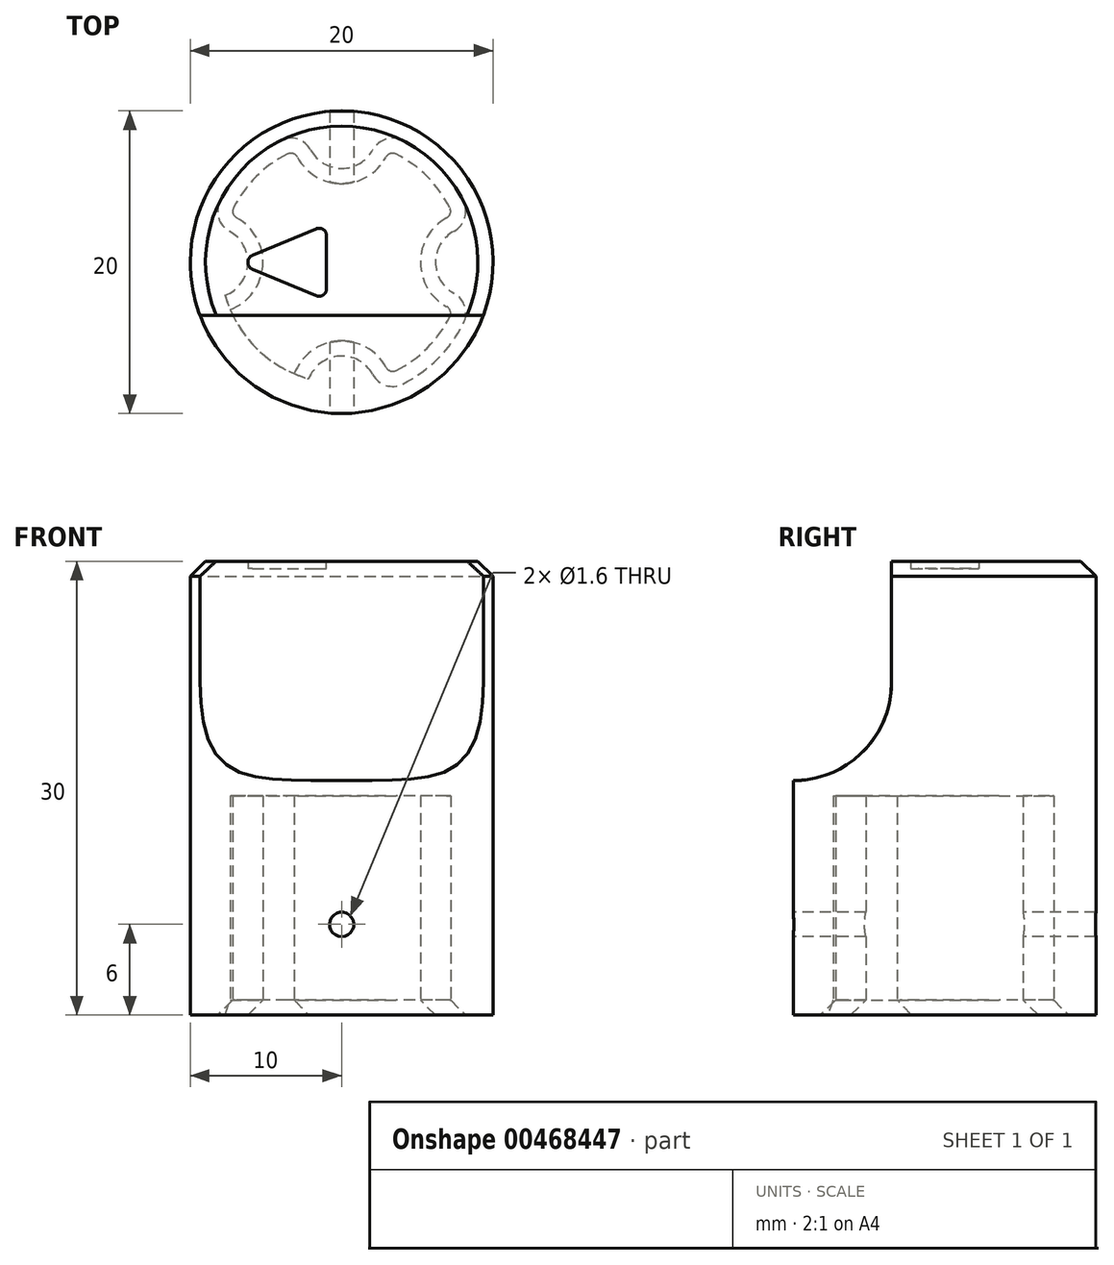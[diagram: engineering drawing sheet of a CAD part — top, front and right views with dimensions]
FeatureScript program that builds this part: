
annotation { "Feature Type Name" : "Feature", "Feature Type Description" : "" }
export const myFeature = defineFeature(function(context is Context, id is Id, definition is map)
    precondition{}
    {
        {
            var Q0;
            Q0=qCreatedBy(makeId("Right.planeOp"),FACE);
            var sketch = newSketch(context, id + "F0", { "sketchPlane" : qUnion([Q0])});
            skLineSegment(sketch, "E0", {"start": v(-8, 0) * mm, "end": v(-8, 14.5) * mm});
            skLineSegment(sketch, "E1", {"start": v(-8, 14.5) * mm, "end": v(0, 14.5) * mm});
            skLineSegment(sketch, "E2", {"start": v(0, 14.5) * mm, "end": v(0, 30) * mm});
            skLineSegment(sketch, "E3", {"start": v(0, 30) * mm, "end": v(-10, 30) * mm});
            skLineSegment(sketch, "E4", {"start": v(-10, 30) * mm, "end": v(-10, 0) * mm});
            skLineSegment(sketch, "E5", {"start": v(-10, 0) * mm, "end": v(-8, 0) * mm});
            skSolve(sketch);
        }
        {
            var Q0;
            Q0=qSketchRegion(id+"F0",true);
            var Q1;
            Q1=sQuery(id+"F0.wireOp",EDGE,"E2");
            revolve(context, id + "F1", {"surfaceOperationType" : NewSurfaceOperationType.NEW, "entities" : qUnion([Q0]), "axis" : qUnion([Q1]), "revolveType" : RevolveType.FULL});
        }
        {
            var Q0;
            Q0=qCreatedBy(makeId("Right.planeOp"),FACE);
            var sketch = newSketch(context, id + "F2", { "sketchPlane" : qUnion([Q0])});
            skLineSegment(sketch, "E6", {"start": v(-3.5, 30) * mm, "end": v(-3.5, 22) * mm});
            skArc(sketch, "E7", {"start": v(-10, 15.5) * mm, "mid": v(-5.4, 17.4) * mm, "end": v(-3.5, 22) * mm});
            skLineSegment(sketch, "E8", {"start": v(-10, 15.5) * mm, "end": v(-10, 30) * mm});
            skLineSegment(sketch, "E9", {"start": v(-10, 30) * mm, "end": v(-3.5, 30) * mm});
            skSolve(sketch);
        }
        {
            var Q0;
            Q0=qSketchRegion(id+"F2",true);
            extrude(context, id + "F3", {"entities" : qUnion([Q0]), "operationType" : NewBodyOperationType.REMOVE, "endBound" : BoundingType.SYMMETRIC, "oppositeDirection" : true, "offsetDistance" : 25 * mm, "depth" : 25 * mm});
        }
        {
            var Q0;
            Q0=makeQuery(id+"FGqc0gzjsB6oOKz_1.1.F3.boolean.opBoolean","SPLIT",EDGE,{"disambiguationData":[OD(1.0)],"derivedFrom":makeQuery(id+"F1.opRevolve","SWEPT_EDGE",EDGE,{"disambiguationData":[OSD([sQuery(id+"F0.wireOp",EDGE,"E3"),sQuery(id+"F0.wireOp",EDGE,"E4")])]})});
            var Q1;
            Q1=makeQuery(id+"FGqc0gzjsB6oOKz_1.1.F3.boolean.opBoolean","SPLIT",EDGE,{"disambiguationData":[OD(0.0)],"derivedFrom":makeQuery(id+"F1.opRevolve","SWEPT_EDGE",EDGE,{"disambiguationData":[OSD([sQuery(id+"F0.wireOp",EDGE,"E3"),sQuery(id+"F0.wireOp",EDGE,"E4")])]})});
            chamfer(context, id + "F4", {"entities" : qUnion([Q0, Q1]), "width" : 1 * mm, "tangentPropagation" : true});
        }
        {
            var Q0;
            Q0=makeQuery(id+"F1.opRevolve","SWEPT_FACE",FACE,{"disambiguationData":[OSD([sQuery(id+"F0.wireOp",EDGE,"E5")])]});
            var sketch = newSketch(context, id + "F5", { "sketchPlane" : qUnion([Q0])});
            skArc(sketch, "E10", {"start": v(-7.37, -3.12) * mm, "mid": v(-5.2, 0) * mm, "end": v(-7.37, 3.12) * mm});
            skArc(sketch, "E11", {"start": v(-3.12, 7.37) * mm, "mid": v(0, 5.2) * mm, "end": v(3.12, 7.37) * mm});
            skArc(sketch, "E12", {"start": v(7.37, 3.12) * mm, "mid": v(5.2, 0) * mm, "end": v(7.37, -3.12) * mm});
            skArc(sketch, "E13", {"start": v(3.12, -7.37) * mm, "mid": v(0, -5.2) * mm, "end": v(-3.12, -7.37) * mm});
            skArc(sketch, "E14.0", {"start": v(-7.37, 3.12) * mm, "mid": v(-8, 0) * mm, "end": v(-7.37, -3.12) * mm});
            skArc(sketch, "E15.trimOffspring", {"start": v(3.12, 7.37) * mm, "mid": v(0, 8) * mm, "end": v(-3.12, 7.37) * mm});
            skArc(sketch, "E16.trimOffspring", {"start": v(7.37, -3.12) * mm, "mid": v(8, 0) * mm, "end": v(7.37, 3.12) * mm});
            skArc(sketch, "E17.trimOffspring", {"start": v(-3.12, -7.37) * mm, "mid": v(0, -8) * mm, "end": v(3.12, -7.37) * mm});
            skSolve(sketch);
        }
        {
            var Q0;
            Q0 = qSketchRegion(id + "F5", true);
            extrude(context, id + "F6", {"entities" : qUnion([Q0]), "operationType" : NewBodyOperationType.ADD, "endBound" : BoundingType.UP_TO_NEXT, "oppositeDirection" : true, "depth" : 25 * mm, "offsetDistance" : 25 * mm});
        }
        {
            var Q0;
            {var subQ0=sQuery(id+"F5.wireOp",EDGE,"E15.trimOffspring");var subQ1=sQuery(id+"F5.wireOp",EDGE,"E11");var subQ2=sQuery(id+"F0.wireOp",EDGE,"E5");var subQ3=sQuery(id+"F0.wireOp",EDGE,"E0");Q0=makeQuery(id+"F6.opExtrude","SWEPT_EDGE",EDGE,{"disambiguationData":[OSD([subQ3,subQ2,subQ1,subQ0]),TDD([makeQuery(id+"F5.imprint","INTERSECT",VERTEX,{"disambiguationData":[OD(0.0)],"derivedFrom":[makeQuery(id+"F1.opRevolve","SWEPT_EDGE",EDGE,{"disambiguationData":[OSD([subQ3,subQ2])]}),subQ1,subQ0]})])]});}
            var Q1;
            {var subQ0=sQuery(id+"F5.wireOp",EDGE,"E14.0");var subQ1=sQuery(id+"F5.wireOp",EDGE,"E10");var subQ2=sQuery(id+"F0.wireOp",EDGE,"E5");var subQ3=sQuery(id+"F0.wireOp",EDGE,"E0");Q1=makeQuery(id+"F6.opExtrude","SWEPT_EDGE",EDGE,{"disambiguationData":[OSD([subQ3,subQ2,subQ1,subQ0]),TDD([makeQuery(id+"F5.imprint","INTERSECT",VERTEX,{"disambiguationData":[OD(1.0)],"derivedFrom":[makeQuery(id+"F1.opRevolve","SWEPT_EDGE",EDGE,{"disambiguationData":[OSD([subQ3,subQ2])]}),subQ1,subQ0]})])]});}
            var Q2;
            {var subQ0=sQuery(id+"F5.wireOp",EDGE,"E14.0");var subQ1=sQuery(id+"F5.wireOp",EDGE,"E10");var subQ2=sQuery(id+"F0.wireOp",EDGE,"E5");var subQ3=sQuery(id+"F0.wireOp",EDGE,"E0");Q2=makeQuery(id+"F6.opExtrude","SWEPT_EDGE",EDGE,{"disambiguationData":[OSD([subQ3,subQ2,subQ1,subQ0]),TDD([makeQuery(id+"F5.imprint","INTERSECT",VERTEX,{"disambiguationData":[OD(0.0)],"derivedFrom":[makeQuery(id+"F1.opRevolve","SWEPT_EDGE",EDGE,{"disambiguationData":[OSD([subQ3,subQ2])]}),subQ1,subQ0]})])]});}
            var Q3;
            {var subQ0=sQuery(id+"F5.wireOp",EDGE,"E17.trimOffspring");var subQ1=sQuery(id+"F5.wireOp",EDGE,"E13");var subQ2=sQuery(id+"F0.wireOp",EDGE,"E5");var subQ3=sQuery(id+"F0.wireOp",EDGE,"E0");Q3=makeQuery(id+"F6.opExtrude","SWEPT_EDGE",EDGE,{"disambiguationData":[OSD([subQ3,subQ2,subQ1,subQ0]),TDD([makeQuery(id+"F5.imprint","INTERSECT",VERTEX,{"disambiguationData":[OD(1.0)],"derivedFrom":[makeQuery(id+"F1.opRevolve","SWEPT_EDGE",EDGE,{"disambiguationData":[OSD([subQ3,subQ2])]}),subQ1,subQ0]})])]});}
            var Q4;
            {var subQ0=sQuery(id+"F5.wireOp",EDGE,"E17.trimOffspring");var subQ1=sQuery(id+"F5.wireOp",EDGE,"E13");var subQ2=sQuery(id+"F0.wireOp",EDGE,"E5");var subQ3=sQuery(id+"F0.wireOp",EDGE,"E0");Q4=makeQuery(id+"F6.opExtrude","SWEPT_EDGE",EDGE,{"disambiguationData":[OSD([subQ3,subQ2,subQ1,subQ0]),TDD([makeQuery(id+"F5.imprint","INTERSECT",VERTEX,{"disambiguationData":[OD(0.0)],"derivedFrom":[makeQuery(id+"F1.opRevolve","SWEPT_EDGE",EDGE,{"disambiguationData":[OSD([subQ3,subQ2])]}),subQ1,subQ0]})])]});}
            var Q5;
            {var subQ0=sQuery(id+"F5.wireOp",EDGE,"E16.trimOffspring");var subQ1=sQuery(id+"F5.wireOp",EDGE,"E12");var subQ2=sQuery(id+"F0.wireOp",EDGE,"E5");var subQ3=sQuery(id+"F0.wireOp",EDGE,"E0");Q5=makeQuery(id+"F6.opExtrude","SWEPT_EDGE",EDGE,{"disambiguationData":[OSD([subQ3,subQ2,subQ1,subQ0]),TDD([makeQuery(id+"F5.imprint","INTERSECT",VERTEX,{"disambiguationData":[OD(1.0)],"derivedFrom":[makeQuery(id+"F1.opRevolve","SWEPT_EDGE",EDGE,{"disambiguationData":[OSD([subQ3,subQ2])]}),subQ1,subQ0]})])]});}
            var Q6;
            {var subQ0=sQuery(id+"F5.wireOp",EDGE,"E16.trimOffspring");var subQ1=sQuery(id+"F5.wireOp",EDGE,"E12");var subQ2=sQuery(id+"F0.wireOp",EDGE,"E5");var subQ3=sQuery(id+"F0.wireOp",EDGE,"E0");Q6=makeQuery(id+"F6.opExtrude","SWEPT_EDGE",EDGE,{"disambiguationData":[OSD([subQ3,subQ2,subQ1,subQ0]),TDD([makeQuery(id+"F5.imprint","INTERSECT",VERTEX,{"disambiguationData":[OD(0.0)],"derivedFrom":[makeQuery(id+"F1.opRevolve","SWEPT_EDGE",EDGE,{"disambiguationData":[OSD([subQ3,subQ2])]}),subQ1,subQ0]})])]});}
            var Q7;
            {var subQ0=sQuery(id+"F5.wireOp",EDGE,"E15.trimOffspring");var subQ1=sQuery(id+"F5.wireOp",EDGE,"E11");var subQ2=sQuery(id+"F0.wireOp",EDGE,"E5");var subQ3=sQuery(id+"F0.wireOp",EDGE,"E0");Q7=makeQuery(id+"F6.opExtrude","SWEPT_EDGE",EDGE,{"disambiguationData":[OSD([subQ3,subQ2,subQ1,subQ0]),TDD([makeQuery(id+"F5.imprint","INTERSECT",VERTEX,{"disambiguationData":[OD(1.0)],"derivedFrom":[makeQuery(id+"F1.opRevolve","SWEPT_EDGE",EDGE,{"disambiguationData":[OSD([subQ3,subQ2])]}),subQ1,subQ0]})])]});}
            fillet(context, id + "F7", {"entities" : qUnion([Q0, Q1, Q2, Q3, Q4, Q5, Q6, Q7]), "tangentPropagation" : true, "radius" : .5 * mm, "defaultsChanged" : true, "vertexSettings" : [], "allowEdgeOverflow" : false});
        }
        {
            var Q0;
            Q0=qCreatedBy(makeId("Front.planeOp"),FACE);
            var sketch = newSketch(context, id + "F8", { "sketchPlane" : qUnion([Q0])});
            skCircle(sketch, "E18", {"center": v(0, 6) * mm, "radius": 0.8 * mm});
            skSolve(sketch);
        }
        {
            var Q0;
            Q0=qSketchRegion(id+"F8",true);
            extrude(context, id + "F9", {"entities" : qUnion([Q0]), "operationType" : NewBodyOperationType.REMOVE, "endBound" : BoundingType.SYMMETRIC, "oppositeDirection" : true, "depth" : 25 * mm, "hasSecondDirection" : true, "secondDirectionBound" : SecondDirectionBoundingType.UP_TO_NEXT, "secondDirectionOppositeDirection" : true, "secondDirectionDepth" : 25 * mm});
        }
        {
            var Q0;
            {var subQ0=sQuery(id+"F5.wireOp",EDGE,"E10");var subQ1=sQuery(id+"F0.wireOp",EDGE,"E5");var subQ2=sQuery(id+"F5.wireOp",EDGE,"E13");var subQ3=sQuery(id+"F0.wireOp",EDGE,"E0");Q0=makeQuery(id+"F6.boolean.opBoolean","SPLIT",EDGE,{"disambiguationData":[TD([makeQuery(id+"F1.opRevolve","SWEPT_FACE",FACE,{"disambiguationData":[OSD([subQ3])]}),makeQuery(id+"F1.opRevolve","SWEPT_FACE",FACE,{"disambiguationData":[OSD([subQ1])]}),makeQuery(id+"F6.opExtrude","SWEPT_FACE",FACE,{"disambiguationData":[OSD([subQ0])]}),makeQuery(id+"F6.opExtrude","CAP_FACE",FACE,{"disambiguationData":[OSD([subQ0,sQuery(id+"F5.wireOp",EDGE,"E14.0")])],"isStart":true}),makeQuery(id+"F6.opExtrude","CAP_FACE",FACE,{"disambiguationData":[OSD([sQuery(id+"F5.wireOp",EDGE,"E11"),sQuery(id+"F5.wireOp",EDGE,"E15.trimOffspring")])],"isStart":true}),makeQuery(id+"F6.opExtrude","CAP_FACE",FACE,{"disambiguationData":[OSD([sQuery(id+"F5.wireOp",EDGE,"E12"),sQuery(id+"F5.wireOp",EDGE,"E16.trimOffspring")])],"isStart":true}),makeQuery(id+"F6.opExtrude","SWEPT_FACE",FACE,{"disambiguationData":[OSD([subQ2])]}),makeQuery(id+"F6.opExtrude","CAP_FACE",FACE,{"disambiguationData":[OSD([subQ2,sQuery(id+"F5.wireOp",EDGE,"E17.trimOffspring")])],"isStart":true})])],"derivedFrom":makeQuery(id+"F1.opRevolve","SWEPT_EDGE",EDGE,{"disambiguationData":[OSD([subQ3,subQ1])]})});}
            chamfer(context, id + "F10", {"entities" : qUnion([Q0]), "width" : 1 * mm, "tangentPropagation" : true});
        }
        {
            var Q0;
            Q0=makeQuery(id+"F1.opRevolve","SWEPT_FACE",FACE,{"disambiguationData":[OSD([sQuery(id+"F0.wireOp",EDGE,"E3")])]});
            var sketch = newSketch(context, id + "F11", { "sketchPlane" : qUnion([Q0])});
            skLineSegment(sketch, "E19", {"start": v(-7, 0) * mm, "end": v(-1, 2.5) * mm});
            skLineSegment(sketch, "E20", {"start": v(-1, 2.5) * mm, "end": v(-1, -2.5) * mm});
            skLineSegment(sketch, "E21", {"start": v(-1, -2.5) * mm, "end": v(-7, 0) * mm});
            skLineSegment(sketch, "E22", {"start": v(0, 0) * mm, "end": v(-1, 0) * mm, "construction": true});
            skSolve(sketch);
        }
        {
            var Q0;
            Q0=qSketchRegion(id+"F11",true);
            extrude(context, id + "F12", {"entities" : qUnion([Q0]), "operationType" : NewBodyOperationType.REMOVE, "oppositeDirection" : true, "depth" : .5 * mm});
        }
        {
            var Q0;
            Q0=makeQuery(id+"F12.boolean.opBoolean","COPY",EDGE,{"derivedFrom":makeQuery(id+"F12.opExtrude","SWEPT_EDGE",EDGE,{"disambiguationData":[OSD([sQuery(id+"F11.wireOp",EDGE,"E19"),sQuery(id+"F11.wireOp",EDGE,"E20")])]})});
            var Q1;
            Q1=makeQuery(id+"F12.boolean.opBoolean","COPY",EDGE,{"derivedFrom":makeQuery(id+"F12.opExtrude","SWEPT_EDGE",EDGE,{"disambiguationData":[OSD([sQuery(id+"F11.wireOp",EDGE,"E20"),sQuery(id+"F11.wireOp",EDGE,"E21")])]})});
            var Q2;
            Q2=makeQuery(id+"F12.boolean.opBoolean","COPY",EDGE,{"derivedFrom":makeQuery(id+"F12.opExtrude","SWEPT_EDGE",EDGE,{"disambiguationData":[OSD([sQuery(id+"F11.wireOp",EDGE,"E19"),sQuery(id+"F11.wireOp",EDGE,"E21")])]})});
            fillet(context, id + "F13", {"entities" : qUnion([Q0, Q1, Q2]), "radius" : .5 * mm, "tangentPropagation" : true, "allowEdgeOverflow" : false});
        }
    });
